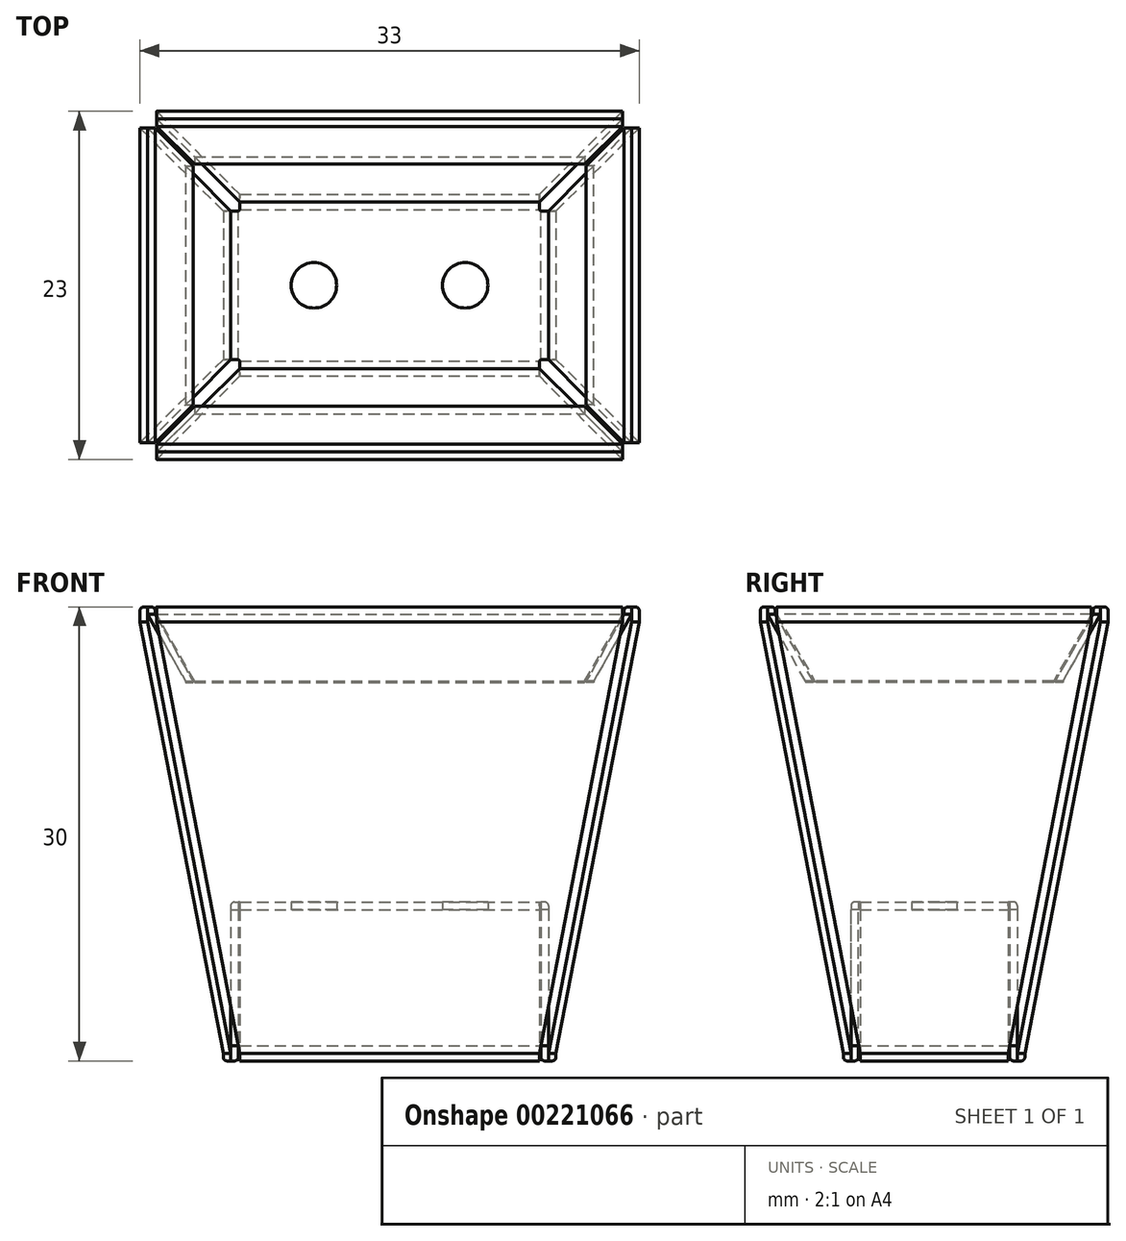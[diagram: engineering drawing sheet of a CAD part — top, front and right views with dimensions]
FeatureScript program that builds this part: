
annotation { "Feature Type Name" : "Feature", "Feature Type Description" : "" }
export const myFeature = defineFeature(function(context is Context, id is Id, definition is map)
    precondition{}
    {
        {
            var Q0;
            Q0=qCreatedBy(makeId("Top.planeOp"),FACE);
            var sketch = newSketch(context, id + "F0", { "sketchPlane" : qUnion([Q0])});
            skLineSegment(sketch, "E0.bottom", {"start": v(-9.9, 5) * mm, "end": v(9.9, 5) * mm});
            skLineSegment(sketch, "E0.left", {"start": v(-10, 4.9) * mm, "end": v(-10, -4.9) * mm});
            skLineSegment(sketch, "E0.right", {"start": v(10, 4.9) * mm, "end": v(10, -4.9) * mm});
            skCircle(sketch, "E1", {"center": v(-5, 0) * mm, "radius": 1.5 * mm});
            skCircle(sketch, "E2", {"center": v(5, 0) * mm, "radius": 1.5 * mm});
            skLineSegment(sketch, "E3", {"start": v(-9.9, 5.5) * mm, "end": v(9.9, 5.5) * mm});
            skLineSegment(sketch, "E4", {"start": v(-10.5, -4.9) * mm, "end": v(-10.5, 4.9) * mm});
            skLineSegment(sketch, "E5", {"start": v(10.5, 4.9) * mm, "end": v(10.5, -4.9) * mm});
            skLineSegment(sketch, "E6", {"start": v(-10.5, -4.9) * mm, "end": v(-10, -4.9) * mm});
            skLineSegment(sketch, "E7", {"start": v(-10.5, 4.9) * mm, "end": v(-10, 4.9) * mm});
            skLineSegment(sketch, "E8", {"start": v(-9.9, 5.5) * mm, "end": v(-9.9, 5) * mm});
            skPoint(sketch, "E9", {"position": v(-9.9, 5) * mm});
            skPoint(sketch, "E10", {"position": v(-10, 4.9) * mm});
            skLineSegment(sketch, "E11", {"start": v(-9.9, 5) * mm, "end": v(-10, 4.9) * mm});
            skLineSegment(sketch, "E12", {"start": v(9.9, 5.5) * mm, "end": v(9.9, 5) * mm});
            skLineSegment(sketch, "E13", {"start": v(9.9, 5) * mm, "end": v(10, 4.9) * mm});
            skLineSegment(sketch, "E14", {"start": v(10, 4.9) * mm, "end": v(10.5, 4.9) * mm});
            skLineSegment(sketch, "E15", {"start": v(10.5, -4.9) * mm, "end": v(10, -4.9) * mm});
            skLineSegment(sketch, "E16", {"start": v(9.9, -5) * mm, "end": v(-9.9, -5) * mm});
            skLineSegment(sketch, "E17", {"start": v(-9.9, -5.5) * mm, "end": v(9.9, -5.5) * mm});
            skLineSegment(sketch, "E18", {"start": v(-9.9, -5) * mm, "end": v(-9.9, -5.5) * mm});
            skLineSegment(sketch, "E19", {"start": v(9.9, -5.5) * mm, "end": v(9.9, -5) * mm});
            skLineSegment(sketch, "E20", {"start": v(9.9, -5) * mm, "end": v(10, -4.9) * mm});
            skLineSegment(sketch, "E21", {"start": v(-10, -4.9) * mm, "end": v(-9.9, -5) * mm});
            skSolve(sketch);
        }
        {
            var Q0;
            Q0 = qSketchRegion(id + "F0", true);
            extrude(context, id + "F1", {"entities" : qUnion([Q0]), "depth" : 0.5 * mm});
        }
        {
            var Q0;
            Q0=qCreatedBy(makeId("Top.planeOp"),FACE);
            var sketch = newSketch(context, id + "F2", { "sketchPlane" : qUnion([Q0])});
            skLineSegment(sketch, "E22.bottom", {"start": v(-15.4, 11) * mm, "end": v(15.4, 11) * mm});
            skLineSegment(sketch, "E22.top", {"start": v(-15.4, 10.5) * mm, "end": v(15.4, 10.5) * mm});
            skLineSegment(sketch, "E22.left", {"start": v(-15.4, 11) * mm, "end": v(-15.4, 10.5) * mm});
            skLineSegment(sketch, "E22.right", {"start": v(15.4, 11) * mm, "end": v(15.4, 10.5) * mm});
            skLineSegment(sketch, "E23.bottom", {"start": v(-16, 10.4) * mm, "end": v(-15.5, 10.4) * mm});
            skLineSegment(sketch, "E23.top", {"start": v(-16, -10.4) * mm, "end": v(-15.5, -10.4) * mm});
            skLineSegment(sketch, "E23.left", {"start": v(-16, 10.4) * mm, "end": v(-16, -10.4) * mm});
            skLineSegment(sketch, "E23.right", {"start": v(-15.5, 10.4) * mm, "end": v(-15.5, -10.4) * mm});
            skLineSegment(sketch, "E24.bottom", {"start": v(-15.4, -10.5) * mm, "end": v(15.4, -10.5) * mm});
            skLineSegment(sketch, "E24.top", {"start": v(-15.4, -11) * mm, "end": v(15.4, -11) * mm});
            skLineSegment(sketch, "E24.left", {"start": v(-15.4, -10.5) * mm, "end": v(-15.4, -11) * mm});
            skLineSegment(sketch, "E24.right", {"start": v(15.4, -10.5) * mm, "end": v(15.4, -11) * mm});
            skLineSegment(sketch, "E25.bottom", {"start": v(15.5, 10.4) * mm, "end": v(16, 10.4) * mm});
            skLineSegment(sketch, "E25.top", {"start": v(15.5, -10.4) * mm, "end": v(16, -10.4) * mm});
            skLineSegment(sketch, "E25.left", {"start": v(15.5, 10.4) * mm, "end": v(15.5, -10.4) * mm});
            skLineSegment(sketch, "E25.right", {"start": v(16, 10.4) * mm, "end": v(16, -10.4) * mm});
            skLineSegment(sketch, "E26", {"start": v(-15.4, 11) * mm, "end": v(-15.4, 11.5) * mm});
            skLineSegment(sketch, "E27", {"start": v(-15.4, 11.5) * mm, "end": v(15.4, 11.5) * mm});
            skLineSegment(sketch, "E28", {"start": v(15.4, 11.5) * mm, "end": v(15.4, 11) * mm});
            skLineSegment(sketch, "E29", {"start": v(16, 10.4) * mm, "end": v(16.5, 10.4) * mm});
            skLineSegment(sketch, "E30", {"start": v(16.5, 10.4) * mm, "end": v(16.5, -10.4) * mm});
            skLineSegment(sketch, "E31", {"start": v(16.5, -10.4) * mm, "end": v(16, -10.4) * mm});
            skLineSegment(sketch, "E32", {"start": v(15.4, -11) * mm, "end": v(15.4, -11.5) * mm});
            skLineSegment(sketch, "E33", {"start": v(15.4, -11.5) * mm, "end": v(-15.4, -11.5) * mm});
            skLineSegment(sketch, "E34", {"start": v(-15.4, -11.5) * mm, "end": v(-15.4, -11) * mm});
            skLineSegment(sketch, "E35", {"start": v(-16, -10.4) * mm, "end": v(-16.5, -10.4) * mm});
            skLineSegment(sketch, "E36", {"start": v(-16.5, -10.4) * mm, "end": v(-16.5, 10.4) * mm});
            skLineSegment(sketch, "E37", {"start": v(-16.5, 10.4) * mm, "end": v(-16, 10.4) * mm});
            skSolve(sketch);
        }
        {
            var Q0;
            Q0=makeQuery(id+"F1.opExtrude","CAP_FACE",FACE,{"disambiguationData":[OSD([sQuery(id+"F0.wireOp",EDGE,"E1"),sQuery(id+"F0.wireOp",EDGE,"E2"),sQuery(id+"F0.wireOp",EDGE,"E3"),sQuery(id+"F0.wireOp",EDGE,"E4"),sQuery(id+"F0.wireOp",EDGE,"E5"),sQuery(id+"F0.wireOp",EDGE,"E6"),sQuery(id+"F0.wireOp",EDGE,"E7"),sQuery(id+"F0.wireOp",EDGE,"E8"),sQuery(id+"F0.wireOp",EDGE,"E11"),sQuery(id+"F0.wireOp",EDGE,"E12"),sQuery(id+"F0.wireOp",EDGE,"E13"),sQuery(id+"F0.wireOp",EDGE,"E14"),sQuery(id+"F0.wireOp",EDGE,"E15"),sQuery(id+"F0.wireOp",EDGE,"E17"),sQuery(id+"F0.wireOp",EDGE,"E18"),sQuery(id+"F0.wireOp",EDGE,"E19"),sQuery(id+"F0.wireOp",EDGE,"E20"),sQuery(id+"F0.wireOp",EDGE,"E21")])],"isStart":true});
            var sketch = newSketch(context, id + "F3", { "sketchPlane" : qUnion([Q0])});
            skLineSegment(sketch, "E38.bottom", {"start": v(-9.9, 6) * mm, "end": v(9.9, 6) * mm});
            skLineSegment(sketch, "E38.top", {"start": v(-9.9, 5.5) * mm, "end": v(9.9, 5.5) * mm});
            skLineSegment(sketch, "E38.left", {"start": v(-9.9, 6) * mm, "end": v(-9.9, 5.5) * mm});
            skLineSegment(sketch, "E38.right", {"start": v(9.9, 6) * mm, "end": v(9.9, 5.5) * mm});
            skLineSegment(sketch, "E39.top", {"start": v(-9.9, 5) * mm, "end": v(9.9, 5) * mm});
            skLineSegment(sketch, "E39.left", {"start": v(-9.9, 5.5) * mm, "end": v(-9.9, 5) * mm});
            skLineSegment(sketch, "E39.right", {"start": v(9.9, 5.5) * mm, "end": v(9.9, 5) * mm});
            skLineSegment(sketch, "E40.bottom", {"start": v(-9.9, -5) * mm, "end": v(9.9, -5) * mm});
            skLineSegment(sketch, "E40.top", {"start": v(-9.9, -5.5) * mm, "end": v(9.9, -5.5) * mm});
            skLineSegment(sketch, "E40.left", {"start": v(-9.9, -5) * mm, "end": v(-9.9, -5.5) * mm});
            skLineSegment(sketch, "E40.right", {"start": v(9.9, -5) * mm, "end": v(9.9, -5.5) * mm});
            skLineSegment(sketch, "E41.top", {"start": v(-9.9, -6) * mm, "end": v(9.9, -6) * mm});
            skLineSegment(sketch, "E41.left", {"start": v(-9.9, -5.5) * mm, "end": v(-9.9, -6) * mm});
            skLineSegment(sketch, "E41.right", {"start": v(9.9, -5.5) * mm, "end": v(9.9, -6) * mm});
            skLineSegment(sketch, "E42.bottom", {"start": v(-10, 4.9) * mm, "end": v(-10.5, 4.9) * mm});
            skLineSegment(sketch, "E42.top", {"start": v(-10, -4.9) * mm, "end": v(-10.5, -4.9) * mm});
            skLineSegment(sketch, "E42.left", {"start": v(-10, 4.9) * mm, "end": v(-10, -4.9) * mm});
            skLineSegment(sketch, "E42.right", {"start": v(-10.5, 4.9) * mm, "end": v(-10.5, -4.9) * mm});
            skLineSegment(sketch, "E43.bottom", {"start": v(-10.5, -4.9) * mm, "end": v(-11, -4.9) * mm});
            skLineSegment(sketch, "E43.top", {"start": v(-10.5, 4.9) * mm, "end": v(-11, 4.9) * mm});
            skLineSegment(sketch, "E43.left", {"start": v(-10.5, -4.9) * mm, "end": v(-10.5, 4.9) * mm});
            skLineSegment(sketch, "E43.right", {"start": v(-11, -4.9) * mm, "end": v(-11, 4.9) * mm});
            skLineSegment(sketch, "E44.bottom", {"start": v(10, 4.9) * mm, "end": v(10.5, 4.9) * mm});
            skLineSegment(sketch, "E44.top", {"start": v(10, -4.9) * mm, "end": v(10.5, -4.9) * mm});
            skLineSegment(sketch, "E44.left", {"start": v(10, 4.9) * mm, "end": v(10, -4.9) * mm});
            skLineSegment(sketch, "E44.right", {"start": v(10.5, 4.9) * mm, "end": v(10.5, -4.9) * mm});
            skLineSegment(sketch, "E45.bottom", {"start": v(10.5, -4.9) * mm, "end": v(11, -4.9) * mm});
            skLineSegment(sketch, "E45.top", {"start": v(10.5, 4.9) * mm, "end": v(11, 4.9) * mm});
            skLineSegment(sketch, "E45.left", {"start": v(10.5, -4.9) * mm, "end": v(10.5, 4.9) * mm});
            skLineSegment(sketch, "E45.right", {"start": v(11, -4.9) * mm, "end": v(11, 4.9) * mm});
            skSolve(sketch);
        }
        {
            var Q0;
            Q0=makeQuery(id+"F3.imprint","IMPRINT",FACE,{"disambiguationData":[TD([[makeQuery(id+"F3.imprint","IMPRINT",EDGE,{"derivedFrom":sQuery(id+"F3.wireOp",EDGE,"E44.bottom")}),1.0]])]});
            var Q1;
            Q1=makeQuery(id+"F3.imprint","IMPRINT",FACE,{"disambiguationData":[TD([[makeQuery(id+"F3.imprint","IMPRINT",EDGE,{"derivedFrom":sQuery(id+"F3.wireOp",EDGE,"E40.bottom")}),-1.0]])]});
            var Q2;
            Q2=makeQuery(id+"F3.imprint","IMPRINT",FACE,{"disambiguationData":[TD([[makeQuery(id+"F3.imprint","IMPRINT",EDGE,{"derivedFrom":sQuery(id+"F3.wireOp",EDGE,"E38.top")}),-1.0]])]});
            var Q3;
            Q3=makeQuery(id+"F3.imprint","IMPRINT",FACE,{"disambiguationData":[TD([[makeQuery(id+"F3.imprint","IMPRINT",EDGE,{"derivedFrom":sQuery(id+"F3.wireOp",EDGE,"E42.bottom")}),1.0]])]});
            var Q4;
            Q4=makeQuery(id+"F3.imprint","IMPRINT",FACE,{"disambiguationData":[TD([[makeQuery(id+"F3.imprint","IMPRINT",EDGE,{"derivedFrom":sQuery(id+"F3.wireOp",EDGE,"E42.bottom")}),-1.0]])]});
            extrude(context, id + "F4", {"entities" : qUnion([Q0, Q1, Q2, Q3, Q4]), "oppositeDirection" : true, "depth" : 1 * mm});
        }
        {
            var Q0;
            Q0=makeQuery(id+"F3.imprint","IMPRINT",FACE,{"disambiguationData":[TD([[makeQuery(id+"F3.imprint","IMPRINT",EDGE,{"derivedFrom":sQuery(id+"F3.wireOp",EDGE,"E40.top")}),-1.0]])]});
            var Q1;
            Q1=makeQuery(id+"F3.imprint","IMPRINT",FACE,{"disambiguationData":[TD([[makeQuery(id+"F3.imprint","IMPRINT",EDGE,{"derivedFrom":sQuery(id+"F3.wireOp",EDGE,"E38.bottom")}),-1.0]])]});
            var Q2;
            Q2=makeQuery(id+"F3.imprint","IMPRINT",FACE,{"disambiguationData":[TD([[makeQuery(id+"F3.imprint","IMPRINT",EDGE,{"derivedFrom":sQuery(id+"F3.wireOp",EDGE,"E43.bottom")}),-1.0]])]});
            var Q3;
            Q3=makeQuery(id+"F3.imprint","IMPRINT",FACE,{"disambiguationData":[TD([[makeQuery(id+"F3.imprint","IMPRINT",EDGE,{"derivedFrom":sQuery(id+"F3.wireOp",EDGE,"E45.bottom")}),1.0]])]});
            extrude(context, id + "F5", {"entities" : qUnion([Q0, Q1, Q2, Q3]), "oppositeDirection" : true, "depth" : 0.5 * mm});
        }
        {
            var Q0;
            Q0=makeQuery(id+"F4.opExtrude","SWEPT_BODY",BODY,{"disambiguationData":[OSD([sQuery(id+"F3.wireOp",EDGE,"E38.top"),sQuery(id+"F3.wireOp",EDGE,"E39.top"),sQuery(id+"F3.wireOp",EDGE,"E39.left"),sQuery(id+"F3.wireOp",EDGE,"E39.right")])]});
            var Q1;
            Q1=makeQuery(id+"F5.opExtrude","SWEPT_BODY",BODY,{"disambiguationData":[OSD([sQuery(id+"F3.wireOp",EDGE,"E38.bottom"),sQuery(id+"F3.wireOp",EDGE,"E38.left"),sQuery(id+"F3.wireOp",EDGE,"E38.right"),sQuery(id+"F3.wireOp",EDGE,"E38.top")])]});
            var Q2;
            Q2=makeQuery(id+"F5.opExtrude","SWEPT_BODY",BODY,{"disambiguationData":[OSD([sQuery(id+"F3.wireOp",EDGE,"E45.bottom"),sQuery(id+"F3.wireOp",EDGE,"E45.top"),sQuery(id+"F3.wireOp",EDGE,"E45.left"),sQuery(id+"F3.wireOp",EDGE,"E45.right")])]});
            var Q3;
            Q3=makeQuery(id+"F4.opExtrude","SWEPT_BODY",BODY,{"disambiguationData":[OSD([sQuery(id+"F3.wireOp",EDGE,"E44.bottom"),sQuery(id+"F3.wireOp",EDGE,"E44.top"),sQuery(id+"F3.wireOp",EDGE,"E44.left"),sQuery(id+"F3.wireOp",EDGE,"E45.left")])]});
            var Q4;
            Q4=makeQuery(id+"F5.opExtrude","SWEPT_BODY",BODY,{"disambiguationData":[OSD([sQuery(id+"F3.wireOp",EDGE,"E40.top"),sQuery(id+"F3.wireOp",EDGE,"E41.top"),sQuery(id+"F3.wireOp",EDGE,"E41.left"),sQuery(id+"F3.wireOp",EDGE,"E41.right")])]});
            var Q5;
            Q5=makeQuery(id+"F4.opExtrude","SWEPT_BODY",BODY,{"disambiguationData":[OSD([sQuery(id+"F3.wireOp",EDGE,"E40.bottom"),sQuery(id+"F3.wireOp",EDGE,"E40.left"),sQuery(id+"F3.wireOp",EDGE,"E40.right"),sQuery(id+"F3.wireOp",EDGE,"E40.top")])]});
            var Q6;
            Q6=makeQuery(id+"F5.opExtrude","SWEPT_BODY",BODY,{"disambiguationData":[OSD([sQuery(id+"F3.wireOp",EDGE,"E43.bottom"),sQuery(id+"F3.wireOp",EDGE,"E43.top"),sQuery(id+"F3.wireOp",EDGE,"E43.left"),sQuery(id+"F3.wireOp",EDGE,"E43.right")])]});
            var Q7;
            Q7=makeQuery(id+"F4.opExtrude","SWEPT_BODY",BODY,{"disambiguationData":[OSD([sQuery(id+"F3.wireOp",EDGE,"E42.bottom"),sQuery(id+"F3.wireOp",EDGE,"E42.top"),sQuery(id+"F3.wireOp",EDGE,"E42.left"),sQuery(id+"F3.wireOp",EDGE,"E43.left")])]});
            transform(context, id + "F6", {"entities" : qUnion([Q0, Q1, Q2, Q3, Q4, Q5, Q6, Q7]), "transformType" : TransformType.TRANSLATION_3D, "dx" : 0 * mm, "dy" : 0 * mm, "dz" : -10 * mm, "makeCopy" : false});
        }
        {
            var Q0;
            Q0=makeQuery(id+"F4.opExtrude","CAP_FACE",FACE,{"disambiguationData":[OSD([sQuery(id+"F3.wireOp",EDGE,"E38.top"),sQuery(id+"F3.wireOp",EDGE,"E39.top"),sQuery(id+"F3.wireOp",EDGE,"E39.left"),sQuery(id+"F3.wireOp",EDGE,"E39.right")])],"isStart":false});
            var Q1;
            Q1=makeQuery(id+"F0.imprint","IMPRINT",FACE,{"disambiguationData":[TD([[makeQuery(id+"F0.imprint","IMPRINT",EDGE,{"derivedFrom":sQuery(id+"F0.wireOp",EDGE,"E16")}),1.0]])]});
            loft(context, id + "F7", {"sheetProfilesArray" : [{ "sheetProfileEntities" : qUnion([Q0]) }, { "sheetProfileEntities" : qUnion([Q1]) }]});
        }
        {
            var Q0;
            Q0=makeQuery(id+"F0.imprint","IMPRINT",FACE,{"disambiguationData":[TD([[makeQuery(id+"F0.imprint","IMPRINT",EDGE,{"derivedFrom":sQuery(id+"F0.wireOp",EDGE,"E0.right")}),1.0]])]});
            var Q1;
            Q1=makeQuery(id+"F4.opExtrude","CAP_FACE",FACE,{"disambiguationData":[OSD([sQuery(id+"F3.wireOp",EDGE,"E44.bottom"),sQuery(id+"F3.wireOp",EDGE,"E44.top"),sQuery(id+"F3.wireOp",EDGE,"E44.left"),sQuery(id+"F3.wireOp",EDGE,"E45.left")])],"isStart":false});
            loft(context, id + "F8", {"sheetProfilesArray" : [{ "sheetProfileEntities" : qUnion([Q0]) }, { "sheetProfileEntities" : qUnion([Q1]) }]});
        }
        {
            var Q0;
            Q0=makeQuery(id+"F0.imprint","IMPRINT",FACE,{"disambiguationData":[TD([[makeQuery(id+"F0.imprint","IMPRINT",EDGE,{"derivedFrom":sQuery(id+"F0.wireOp",EDGE,"E0.bottom")}),1.0]])]});
            var Q1;
            Q1=makeQuery(id+"F4.opExtrude","CAP_FACE",FACE,{"disambiguationData":[OSD([sQuery(id+"F3.wireOp",EDGE,"E40.bottom"),sQuery(id+"F3.wireOp",EDGE,"E40.left"),sQuery(id+"F3.wireOp",EDGE,"E40.right"),sQuery(id+"F3.wireOp",EDGE,"E40.top")])],"isStart":false});
            loft(context, id + "F9", {"sheetProfilesArray" : [{ "sheetProfileEntities" : qUnion([Q0]) }, { "sheetProfileEntities" : qUnion([Q1]) }]});
        }
        {
            var Q0;
            Q0=makeQuery(id+"F0.imprint","IMPRINT",FACE,{"disambiguationData":[TD([[makeQuery(id+"F0.imprint","IMPRINT",EDGE,{"derivedFrom":sQuery(id+"F0.wireOp",EDGE,"E0.left")}),-1.0]])]});
            var Q1;
            Q1=makeQuery(id+"F4.opExtrude","CAP_FACE",FACE,{"disambiguationData":[OSD([sQuery(id+"F3.wireOp",EDGE,"E42.bottom"),sQuery(id+"F3.wireOp",EDGE,"E42.top"),sQuery(id+"F3.wireOp",EDGE,"E42.left"),sQuery(id+"F3.wireOp",EDGE,"E43.left")])],"isStart":false});
            loft(context, id + "F10", {"sheetProfilesArray" : [{ "sheetProfileEntities" : qUnion([Q0]) }, { "sheetProfileEntities" : qUnion([Q1]) }]});
        }
        {
            var Q0;
            Q0=makeQuery(id+"F1.opExtrude","CAP_EDGE",EDGE,{"disambiguationData":[OSD([sQuery(id+"F0.wireOp",EDGE,"E5")])],"isStart":false});
            var Q1;
            Q1=makeQuery(id+"F1.opExtrude","CAP_EDGE",EDGE,{"disambiguationData":[OSD([sQuery(id+"F0.wireOp",EDGE,"E17")])],"isStart":false});
            var Q2;
            Q2=makeQuery(id+"F1.opExtrude","CAP_EDGE",EDGE,{"disambiguationData":[OSD([sQuery(id+"F0.wireOp",EDGE,"E3")])],"isStart":false});
            var Q3;
            Q3=makeQuery(id+"F1.opExtrude","CAP_EDGE",EDGE,{"disambiguationData":[OSD([sQuery(id+"F0.wireOp",EDGE,"E4")])],"isStart":false});
            var Q4;
            Q4=makeQuery(id+"F5.opExtrude","CAP_EDGE",EDGE,{"disambiguationData":[OSD([sQuery(id+"F3.wireOp",EDGE,"E43.right")])],"isStart":true});
            var Q5;
            Q5=makeQuery(id+"F4.opExtrude","CAP_EDGE",EDGE,{"disambiguationData":[OSD([sQuery(id+"F3.wireOp",EDGE,"E42.left")])],"isStart":true});
            var Q6;
            Q6=makeQuery(id+"F4.opExtrude","CAP_EDGE",EDGE,{"disambiguationData":[OSD([sQuery(id+"F3.wireOp",EDGE,"E39.top")])],"isStart":true});
            var Q7;
            Q7=makeQuery(id+"F5.opExtrude","CAP_EDGE",EDGE,{"disambiguationData":[OSD([sQuery(id+"F3.wireOp",EDGE,"E38.bottom")])],"isStart":true});
            var Q8;
            Q8=makeQuery(id+"F5.opExtrude","CAP_EDGE",EDGE,{"disambiguationData":[OSD([sQuery(id+"F3.wireOp",EDGE,"E41.top")])],"isStart":true});
            var Q9;
            Q9=makeQuery(id+"F4.opExtrude","CAP_EDGE",EDGE,{"disambiguationData":[OSD([sQuery(id+"F3.wireOp",EDGE,"E40.bottom")])],"isStart":true});
            var Q10;
            Q10=makeQuery(id+"F4.opExtrude","CAP_EDGE",EDGE,{"disambiguationData":[OSD([sQuery(id+"F3.wireOp",EDGE,"E44.left")])],"isStart":true});
            var Q11;
            Q11=makeQuery(id+"F5.opExtrude","CAP_EDGE",EDGE,{"disambiguationData":[OSD([sQuery(id+"F3.wireOp",EDGE,"E45.right")])],"isStart":true});
            fillet(context, id + "F11", {"entities" : qUnion([Q0, Q1, Q2, Q3, Q4, Q5, Q6, Q7, Q8, Q9, Q10, Q11]), "radius" : 0.25 * mm, "tangentPropagation" : true, "allowEdgeOverflow" : false});
        }
        {
            var Q0;
            Q0=makeQuery(id+"F2.imprint","IMPRINT",FACE,{"disambiguationData":[TD([[makeQuery(id+"F2.imprint","IMPRINT",EDGE,{"derivedFrom":sQuery(id+"F2.wireOp",EDGE,"E22.bottom")}),1.0]])]});
            var Q1;
            Q1=makeQuery(id+"F2.imprint","IMPRINT",FACE,{"disambiguationData":[TD([[makeQuery(id+"F2.imprint","IMPRINT",EDGE,{"derivedFrom":sQuery(id+"F2.wireOp",EDGE,"E23.left")}),-1.0]])]});
            var Q2;
            Q2=makeQuery(id+"F2.imprint","IMPRINT",FACE,{"disambiguationData":[TD([[makeQuery(id+"F2.imprint","IMPRINT",EDGE,{"derivedFrom":sQuery(id+"F2.wireOp",EDGE,"E24.top")}),-1.0]])]});
            var Q3;
            Q3=makeQuery(id+"F2.imprint","IMPRINT",FACE,{"disambiguationData":[TD([[makeQuery(id+"F2.imprint","IMPRINT",EDGE,{"derivedFrom":sQuery(id+"F2.wireOp",EDGE,"E25.right")}),1.0]])]});
            extrude(context, id + "F12", {"entities" : qUnion([Q0, Q1, Q2, Q3]), "oppositeDirection" : true, "depth" : 1 * mm});
        }
        {
            var Q0;
            Q0=makeQuery(id+"F2.imprint","IMPRINT",FACE,{"disambiguationData":[TD([[makeQuery(id+"F2.imprint","IMPRINT",EDGE,{"derivedFrom":sQuery(id+"F2.wireOp",EDGE,"E23.bottom")}),-1.0]])]});
            var Q1;
            Q1=makeQuery(id+"F2.imprint","IMPRINT",FACE,{"disambiguationData":[TD([[makeQuery(id+"F2.imprint","IMPRINT",EDGE,{"derivedFrom":sQuery(id+"F2.wireOp",EDGE,"E22.bottom")}),-1.0]])]});
            var Q2;
            Q2=makeQuery(id+"F2.imprint","IMPRINT",FACE,{"disambiguationData":[TD([[makeQuery(id+"F2.imprint","IMPRINT",EDGE,{"derivedFrom":sQuery(id+"F2.wireOp",EDGE,"E25.bottom")}),-1.0]])]});
            var Q3;
            Q3=makeQuery(id+"F2.imprint","IMPRINT",FACE,{"disambiguationData":[TD([[makeQuery(id+"F2.imprint","IMPRINT",EDGE,{"derivedFrom":sQuery(id+"F2.wireOp",EDGE,"E24.bottom")}),-1.0]])]});
            extrude(context, id + "F13", {"entities" : qUnion([Q0, Q1, Q2, Q3]), "oppositeDirection" : true, "depth" : 0.5 * mm});
        }
        {
            var Q0;
            Q0=makeQuery(id+"F13.opExtrude","SWEPT_BODY",BODY,{"disambiguationData":[OSD([sQuery(id+"F2.wireOp",EDGE,"E22.bottom"),sQuery(id+"F2.wireOp",EDGE,"E22.top"),sQuery(id+"F2.wireOp",EDGE,"E22.left"),sQuery(id+"F2.wireOp",EDGE,"E22.right")])]});
            var Q1;
            Q1=makeQuery(id+"F12.opExtrude","SWEPT_BODY",BODY,{"disambiguationData":[OSD([sQuery(id+"F2.wireOp",EDGE,"E22.bottom"),sQuery(id+"F2.wireOp",EDGE,"E26"),sQuery(id+"F2.wireOp",EDGE,"E27"),sQuery(id+"F2.wireOp",EDGE,"E28")])]});
            var Q2;
            Q2=makeQuery(id+"F12.opExtrude","SWEPT_BODY",BODY,{"disambiguationData":[OSD([sQuery(id+"F2.wireOp",EDGE,"E23.left"),sQuery(id+"F2.wireOp",EDGE,"E35"),sQuery(id+"F2.wireOp",EDGE,"E36"),sQuery(id+"F2.wireOp",EDGE,"E37")])]});
            var Q3;
            Q3=makeQuery(id+"F13.opExtrude","SWEPT_BODY",BODY,{"disambiguationData":[OSD([sQuery(id+"F2.wireOp",EDGE,"E23.bottom"),sQuery(id+"F2.wireOp",EDGE,"E23.top"),sQuery(id+"F2.wireOp",EDGE,"E23.left"),sQuery(id+"F2.wireOp",EDGE,"E23.right")])]});
            var Q4;
            Q4=makeQuery(id+"F13.opExtrude","SWEPT_BODY",BODY,{"disambiguationData":[OSD([sQuery(id+"F2.wireOp",EDGE,"E24.bottom"),sQuery(id+"F2.wireOp",EDGE,"E24.top"),sQuery(id+"F2.wireOp",EDGE,"E24.left"),sQuery(id+"F2.wireOp",EDGE,"E24.right")])]});
            var Q5;
            Q5=makeQuery(id+"F12.opExtrude","SWEPT_BODY",BODY,{"disambiguationData":[OSD([sQuery(id+"F2.wireOp",EDGE,"E24.top"),sQuery(id+"F2.wireOp",EDGE,"E32"),sQuery(id+"F2.wireOp",EDGE,"E33"),sQuery(id+"F2.wireOp",EDGE,"E34")])]});
            var Q6;
            Q6=makeQuery(id+"F13.opExtrude","SWEPT_BODY",BODY,{"disambiguationData":[OSD([sQuery(id+"F2.wireOp",EDGE,"E25.bottom"),sQuery(id+"F2.wireOp",EDGE,"E25.top"),sQuery(id+"F2.wireOp",EDGE,"E25.left"),sQuery(id+"F2.wireOp",EDGE,"E25.right")])]});
            var Q7;
            Q7=makeQuery(id+"F12.opExtrude","SWEPT_BODY",BODY,{"disambiguationData":[OSD([sQuery(id+"F2.wireOp",EDGE,"E25.right"),sQuery(id+"F2.wireOp",EDGE,"E29"),sQuery(id+"F2.wireOp",EDGE,"E30"),sQuery(id+"F2.wireOp",EDGE,"E31")])]});
            transform(context, id + "F14", {"entities" : qUnion([Q0, Q1, Q2, Q3, Q4, Q5, Q6, Q7]), "transformType" : TransformType.TRANSLATION_3D, "dx" : 0 * mm, "dy" : 0 * mm, "dz" : 20 * mm, "makeCopy" : false});
        }
        {
            var Q0;
            Q0=makeQuery(id+"F5.opExtrude","CAP_FACE",FACE,{"disambiguationData":[OSD([sQuery(id+"F3.wireOp",EDGE,"E43.bottom"),sQuery(id+"F3.wireOp",EDGE,"E43.top"),sQuery(id+"F3.wireOp",EDGE,"E43.left"),sQuery(id+"F3.wireOp",EDGE,"E43.right")])],"isStart":false});
            var Q1;
            Q1=makeQuery(id+"F12.opExtrude","CAP_FACE",FACE,{"disambiguationData":[OSD([sQuery(id+"F2.wireOp",EDGE,"E23.left"),sQuery(id+"F2.wireOp",EDGE,"E35"),sQuery(id+"F2.wireOp",EDGE,"E36"),sQuery(id+"F2.wireOp",EDGE,"E37")])],"isStart":false});
            loft(context, id + "F15", {"sheetProfilesArray" : [{ "sheetProfileEntities" : qUnion([Q0]) }, { "sheetProfileEntities" : qUnion([Q1]) }]});
        }
        {
            var Q0;
            Q0=makeQuery(id+"F5.opExtrude","CAP_FACE",FACE,{"disambiguationData":[OSD([sQuery(id+"F3.wireOp",EDGE,"E38.bottom"),sQuery(id+"F3.wireOp",EDGE,"E38.left"),sQuery(id+"F3.wireOp",EDGE,"E38.right"),sQuery(id+"F3.wireOp",EDGE,"E38.top")])],"isStart":false});
            var Q1;
            Q1=makeQuery(id+"F12.opExtrude","CAP_FACE",FACE,{"disambiguationData":[OSD([sQuery(id+"F2.wireOp",EDGE,"E24.top"),sQuery(id+"F2.wireOp",EDGE,"E32"),sQuery(id+"F2.wireOp",EDGE,"E33"),sQuery(id+"F2.wireOp",EDGE,"E34")])],"isStart":false});
            loft(context, id + "F16", {"sheetProfilesArray" : [{ "sheetProfileEntities" : qUnion([Q0]) }, { "sheetProfileEntities" : qUnion([Q1]) }]});
        }
        {
            var Q0;
            Q0=makeQuery(id+"F5.opExtrude","CAP_FACE",FACE,{"disambiguationData":[OSD([sQuery(id+"F3.wireOp",EDGE,"E45.bottom"),sQuery(id+"F3.wireOp",EDGE,"E45.top"),sQuery(id+"F3.wireOp",EDGE,"E45.left"),sQuery(id+"F3.wireOp",EDGE,"E45.right")])],"isStart":false});
            var Q1;
            Q1=makeQuery(id+"F12.opExtrude","CAP_FACE",FACE,{"disambiguationData":[OSD([sQuery(id+"F2.wireOp",EDGE,"E25.right"),sQuery(id+"F2.wireOp",EDGE,"E29"),sQuery(id+"F2.wireOp",EDGE,"E30"),sQuery(id+"F2.wireOp",EDGE,"E31")])],"isStart":false});
            loft(context, id + "F17", {"sheetProfilesArray" : [{ "sheetProfileEntities" : qUnion([Q0]) }, { "sheetProfileEntities" : qUnion([Q1]) }]});
        }
        {
            var Q0;
            Q0=makeQuery(id+"F5.opExtrude","CAP_FACE",FACE,{"disambiguationData":[OSD([sQuery(id+"F3.wireOp",EDGE,"E40.top"),sQuery(id+"F3.wireOp",EDGE,"E41.top"),sQuery(id+"F3.wireOp",EDGE,"E41.left"),sQuery(id+"F3.wireOp",EDGE,"E41.right")])],"isStart":false});
            var Q1;
            Q1=makeQuery(id+"F12.opExtrude","CAP_FACE",FACE,{"disambiguationData":[OSD([sQuery(id+"F2.wireOp",EDGE,"E22.bottom"),sQuery(id+"F2.wireOp",EDGE,"E26"),sQuery(id+"F2.wireOp",EDGE,"E27"),sQuery(id+"F2.wireOp",EDGE,"E28")])],"isStart":false});
            loft(context, id + "F18", {"sheetProfilesArray" : [{ "sheetProfileEntities" : qUnion([Q0]) }, { "sheetProfileEntities" : qUnion([Q1]) }]});
        }
        {
            var Q0;
            Q0=qCreatedBy(makeId("Top.planeOp"),FACE);
            var sketch = newSketch(context, id + "F19", { "sketchPlane" : qUnion([Q0])});
            skLineSegment(sketch, "E46.bottom", {"start": v(-12.9, 8.5) * mm, "end": v(12.9, 8.5) * mm});
            skLineSegment(sketch, "E46.top", {"start": v(-12.9, 8) * mm, "end": v(12.9, 8) * mm});
            skLineSegment(sketch, "E46.left", {"start": v(-12.9, 8.5) * mm, "end": v(-12.9, 8) * mm});
            skLineSegment(sketch, "E46.right", {"start": v(12.9, 8.5) * mm, "end": v(12.9, 8) * mm});
            skLineSegment(sketch, "E47.bottom", {"start": v(-13.5, 7.9) * mm, "end": v(-13, 7.9) * mm});
            skLineSegment(sketch, "E47.top", {"start": v(-13.5, -7.9) * mm, "end": v(-13, -7.9) * mm});
            skLineSegment(sketch, "E47.left", {"start": v(-13.5, 7.9) * mm, "end": v(-13.5, -7.9) * mm});
            skLineSegment(sketch, "E47.right", {"start": v(-13, 7.9) * mm, "end": v(-13, -7.9) * mm});
            skLineSegment(sketch, "E48.bottom", {"start": v(-12.9, -8) * mm, "end": v(12.9, -8) * mm});
            skLineSegment(sketch, "E48.top", {"start": v(-12.9, -8.5) * mm, "end": v(12.9, -8.5) * mm});
            skLineSegment(sketch, "E48.left", {"start": v(-12.9, -8) * mm, "end": v(-12.9, -8.5) * mm});
            skLineSegment(sketch, "E48.right", {"start": v(12.9, -8) * mm, "end": v(12.9, -8.5) * mm});
            skLineSegment(sketch, "E49.bottom", {"start": v(13.5, -7.9) * mm, "end": v(13, -7.9) * mm});
            skLineSegment(sketch, "E49.top", {"start": v(13.5, 7.9) * mm, "end": v(13, 7.9) * mm});
            skLineSegment(sketch, "E49.left", {"start": v(13.5, -7.9) * mm, "end": v(13.5, 7.9) * mm});
            skLineSegment(sketch, "E49.right", {"start": v(13, -7.9) * mm, "end": v(13, 7.9) * mm});
            skSolve(sketch);
        }
        {
            var Q0;
            Q0=makeQuery(id+"F19.imprint","IMPRINT",FACE,{"disambiguationData":[TD([[makeQuery(id+"F19.imprint","IMPRINT",EDGE,{"derivedFrom":sQuery(id+"F19.wireOp",EDGE,"E47.bottom")}),-1.0]])]});
            var Q1;
            Q1=makeQuery(id+"F19.imprint","IMPRINT",FACE,{"disambiguationData":[TD([[makeQuery(id+"F19.imprint","IMPRINT",EDGE,{"derivedFrom":sQuery(id+"F19.wireOp",EDGE,"E48.bottom")}),-1.0]])]});
            var Q2;
            Q2=makeQuery(id+"F19.imprint","IMPRINT",FACE,{"disambiguationData":[TD([[makeQuery(id+"F19.imprint","IMPRINT",EDGE,{"derivedFrom":sQuery(id+"F19.wireOp",EDGE,"E49.bottom")}),-1.0]])]});
            var Q3;
            Q3=makeQuery(id+"F19.imprint","IMPRINT",FACE,{"disambiguationData":[TD([[makeQuery(id+"F19.imprint","IMPRINT",EDGE,{"derivedFrom":sQuery(id+"F19.wireOp",EDGE,"E46.bottom")}),-1.0]])]});
            extrude(context, id + "F20", {"entities" : qUnion([Q0, Q1, Q2, Q3]), "depth" : 0.1 * mm});
        }
        {
            var Q0;
            Q0=makeQuery(id+"F20.opExtrude","SWEPT_BODY",BODY,{"disambiguationData":[OSD([sQuery(id+"F19.wireOp",EDGE,"E48.bottom"),sQuery(id+"F19.wireOp",EDGE,"E48.top"),sQuery(id+"F19.wireOp",EDGE,"E48.left"),sQuery(id+"F19.wireOp",EDGE,"E48.right")])]});
            var Q1;
            Q1=makeQuery(id+"F20.opExtrude","SWEPT_BODY",BODY,{"disambiguationData":[OSD([sQuery(id+"F19.wireOp",EDGE,"E46.bottom"),sQuery(id+"F19.wireOp",EDGE,"E46.top"),sQuery(id+"F19.wireOp",EDGE,"E46.left"),sQuery(id+"F19.wireOp",EDGE,"E46.right")])]});
            var Q2;
            Q2=makeQuery(id+"F20.opExtrude","SWEPT_BODY",BODY,{"disambiguationData":[OSD([sQuery(id+"F19.wireOp",EDGE,"E49.bottom"),sQuery(id+"F19.wireOp",EDGE,"E49.top"),sQuery(id+"F19.wireOp",EDGE,"E49.left"),sQuery(id+"F19.wireOp",EDGE,"E49.right")])]});
            var Q3;
            Q3=makeQuery(id+"F20.opExtrude","SWEPT_BODY",BODY,{"disambiguationData":[OSD([sQuery(id+"F19.wireOp",EDGE,"E47.bottom"),sQuery(id+"F19.wireOp",EDGE,"E47.top"),sQuery(id+"F19.wireOp",EDGE,"E47.left"),sQuery(id+"F19.wireOp",EDGE,"E47.right")])]});
            transform(context, id + "F21", {"entities" : qUnion([Q0, Q1, Q2, Q3]), "transformType" : TransformType.TRANSLATION_3D, "dx" : 0 * mm, "dy" : 0 * mm, "dz" : 15 * mm, "makeCopy" : false});
        }
        {
            var Q0;
            Q0=makeQuery(id+"F13.opExtrude","CAP_FACE",FACE,{"disambiguationData":[OSD([sQuery(id+"F2.wireOp",EDGE,"E23.bottom"),sQuery(id+"F2.wireOp",EDGE,"E23.top"),sQuery(id+"F2.wireOp",EDGE,"E23.left"),sQuery(id+"F2.wireOp",EDGE,"E23.right")])],"isStart":false});
            var Q1;
            Q1=makeQuery(id+"F20.opExtrude","CAP_FACE",FACE,{"disambiguationData":[OSD([sQuery(id+"F19.wireOp",EDGE,"E47.bottom"),sQuery(id+"F19.wireOp",EDGE,"E47.top"),sQuery(id+"F19.wireOp",EDGE,"E47.left"),sQuery(id+"F19.wireOp",EDGE,"E47.right")])],"isStart":false});
            loft(context, id + "F22", {"sheetProfilesArray" : [{ "sheetProfileEntities" : qUnion([Q0]) }, { "sheetProfileEntities" : qUnion([Q1]) }]});
        }
        {
            var Q0;
            Q0=makeQuery(id+"F13.opExtrude","CAP_FACE",FACE,{"disambiguationData":[OSD([sQuery(id+"F2.wireOp",EDGE,"E22.bottom"),sQuery(id+"F2.wireOp",EDGE,"E22.top"),sQuery(id+"F2.wireOp",EDGE,"E22.left"),sQuery(id+"F2.wireOp",EDGE,"E22.right")])],"isStart":false});
            var Q1;
            Q1=makeQuery(id+"F20.opExtrude","CAP_FACE",FACE,{"disambiguationData":[OSD([sQuery(id+"F19.wireOp",EDGE,"E46.bottom"),sQuery(id+"F19.wireOp",EDGE,"E46.top"),sQuery(id+"F19.wireOp",EDGE,"E46.left"),sQuery(id+"F19.wireOp",EDGE,"E46.right")])],"isStart":false});
            loft(context, id + "F23", {"sheetProfilesArray" : [{ "sheetProfileEntities" : qUnion([Q0]) }, { "sheetProfileEntities" : qUnion([Q1]) }]});
        }
        {
            var Q0;
            Q0=makeQuery(id+"F20.opExtrude","CAP_FACE",FACE,{"disambiguationData":[OSD([sQuery(id+"F19.wireOp",EDGE,"E48.bottom"),sQuery(id+"F19.wireOp",EDGE,"E48.top"),sQuery(id+"F19.wireOp",EDGE,"E48.left"),sQuery(id+"F19.wireOp",EDGE,"E48.right")])],"isStart":false});
            var Q1;
            Q1=makeQuery(id+"F13.opExtrude","CAP_FACE",FACE,{"disambiguationData":[OSD([sQuery(id+"F2.wireOp",EDGE,"E24.bottom"),sQuery(id+"F2.wireOp",EDGE,"E24.top"),sQuery(id+"F2.wireOp",EDGE,"E24.left"),sQuery(id+"F2.wireOp",EDGE,"E24.right")])],"isStart":false});
            loft(context, id + "F24", {"sheetProfilesArray" : [{ "sheetProfileEntities" : qUnion([Q0]) }, { "sheetProfileEntities" : qUnion([Q1]) }]});
        }
        {
            var Q0;
            Q0=makeQuery(id+"F13.opExtrude","CAP_FACE",FACE,{"disambiguationData":[OSD([sQuery(id+"F2.wireOp",EDGE,"E25.bottom"),sQuery(id+"F2.wireOp",EDGE,"E25.top"),sQuery(id+"F2.wireOp",EDGE,"E25.left"),sQuery(id+"F2.wireOp",EDGE,"E25.right")])],"isStart":false});
            var Q1;
            Q1=makeQuery(id+"F20.opExtrude","CAP_FACE",FACE,{"disambiguationData":[OSD([sQuery(id+"F19.wireOp",EDGE,"E49.bottom"),sQuery(id+"F19.wireOp",EDGE,"E49.top"),sQuery(id+"F19.wireOp",EDGE,"E49.left"),sQuery(id+"F19.wireOp",EDGE,"E49.right")])],"isStart":false});
            loft(context, id + "F25", {"sheetProfilesArray" : [{ "sheetProfileEntities" : qUnion([Q0]) }, { "sheetProfileEntities" : qUnion([Q1]) }]});
        }
        {
            var Q0;
            Q0=makeQuery(id+"F13.opExtrude","CAP_EDGE",EDGE,{"disambiguationData":[OSD([sQuery(id+"F2.wireOp",EDGE,"E23.right")])],"isStart":true});
            fillet(context, id + "F26", {"entities" : qUnion([Q0]), "radius" : 0.25 * mm, "tangentPropagation" : true, "allowEdgeOverflow" : false});
        }
        {
            var Q0;
            Q0=makeQuery(id+"F13.opExtrude","CAP_EDGE",EDGE,{"disambiguationData":[OSD([sQuery(id+"F2.wireOp",EDGE,"E22.top")])],"isStart":true});
            var Q1;
            Q1=makeQuery(id+"F13.opExtrude","CAP_EDGE",EDGE,{"disambiguationData":[OSD([sQuery(id+"F2.wireOp",EDGE,"E25.left")])],"isStart":true});
            var Q2;
            Q2=makeQuery(id+"F13.opExtrude","CAP_EDGE",EDGE,{"disambiguationData":[OSD([sQuery(id+"F2.wireOp",EDGE,"E24.bottom")])],"isStart":true});
            fillet(context, id + "F27", {"entities" : qUnion([Q0, Q1, Q2]), "radius" : 0.25 * mm, "tangentPropagation" : true, "allowEdgeOverflow" : false});
        }
        {
            var Q0;
            Q0=makeQuery(id+"F12.opExtrude","CAP_EDGE",EDGE,{"disambiguationData":[OSD([sQuery(id+"F2.wireOp",EDGE,"E30")])],"isStart":true});
            var Q1;
            Q1=makeQuery(id+"F12.opExtrude","CAP_EDGE",EDGE,{"disambiguationData":[OSD([sQuery(id+"F2.wireOp",EDGE,"E33")])],"isStart":true});
            var Q2;
            Q2=makeQuery(id+"F12.opExtrude","CAP_EDGE",EDGE,{"disambiguationData":[OSD([sQuery(id+"F2.wireOp",EDGE,"E27")])],"isStart":true});
            var Q3;
            Q3=makeQuery(id+"F12.opExtrude","CAP_EDGE",EDGE,{"disambiguationData":[OSD([sQuery(id+"F2.wireOp",EDGE,"E36")])],"isStart":true});
            fillet(context, id + "F28", {"entities" : qUnion([Q0, Q1, Q2, Q3]), "radius" : 0.25 * mm, "tangentPropagation" : true, "allowEdgeOverflow" : false});
        }
    });
